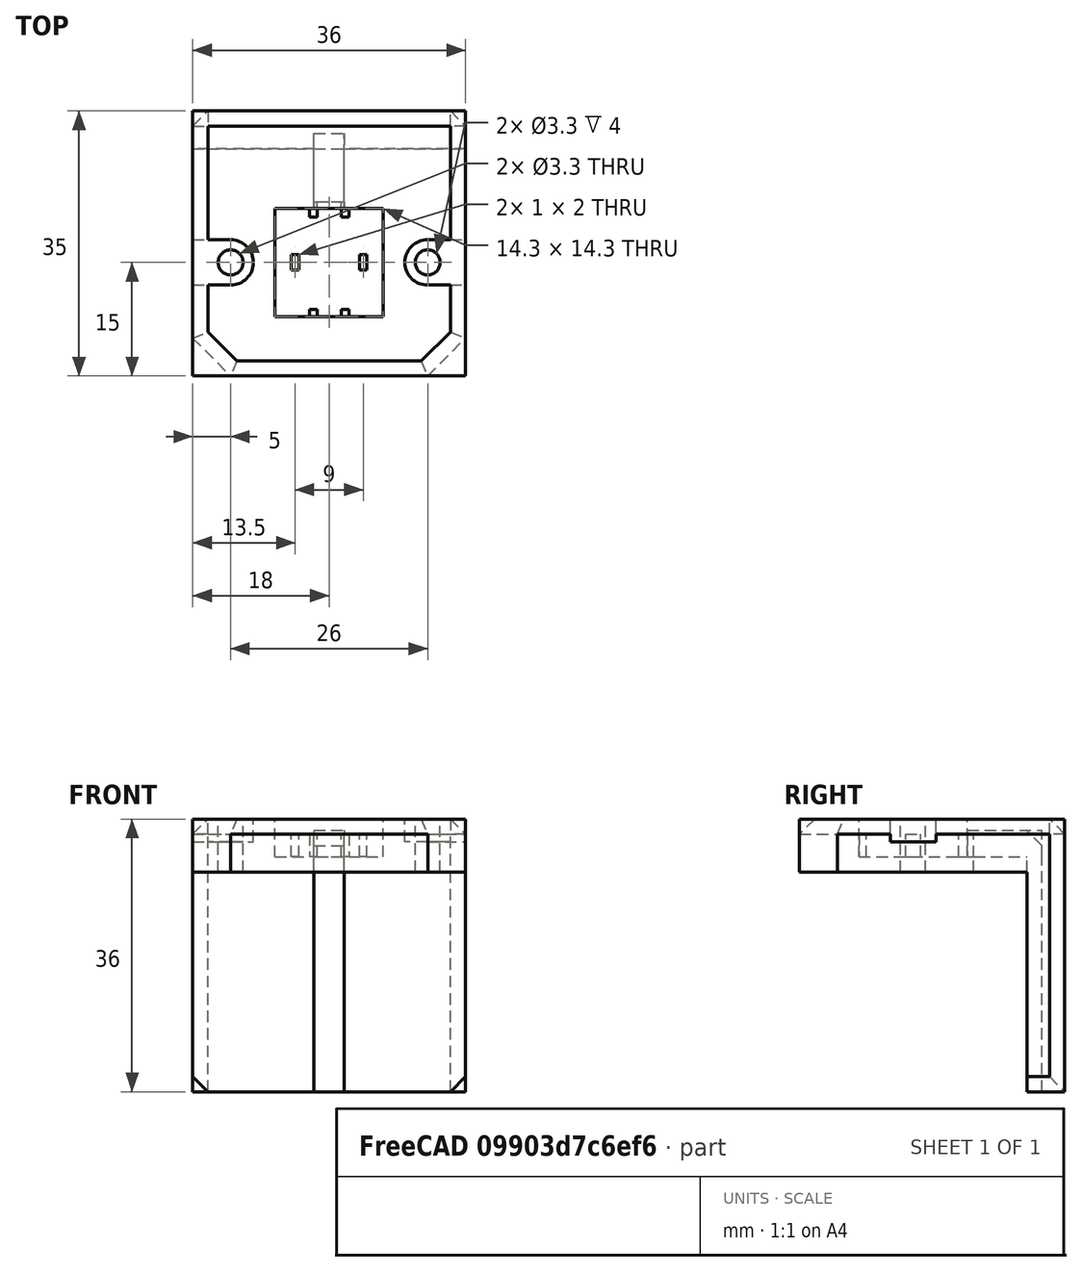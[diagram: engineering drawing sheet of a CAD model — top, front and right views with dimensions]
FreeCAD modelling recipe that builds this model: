
FCSTD DOCUMENT  (FreeCAD 0.18R16146 (Git))
Label: temp-sensor-mount
License: All rights reserved
LicenseURL: http://en.wikipedia.org/wiki/All_rights_reserved
objects: Part::Box×14, Part::MultiFuse×10, Part::Cut×6, Part::Cylinder×4, Part::Chamfer×3, Part::Feature×1
note: 38 computed .brp shape members not serialized (recipe doc carries the construction recipe); baked Part::Feature solids carry a one-line shape summary decoded from their .brp

FEATURE [Part::Box] Box  label="Cube"
  AttacherType = Attacher::AttachEngine3D
  Height = 7
  Length = 36
  Placement = pos=(-18,0,0) rot=(0,0,1;0rad)
  Width = 35
FEATURE [Part::Box] Box001  label="Cube001"
  AttacherType = Attacher::AttachEngine3D
  Height = 36
  Length = 36
  Placement = pos=(-18,30,-29) rot=(0,0,1;0rad)
  Width = 5
FEATURE [Part::Box] Box002  label="Cube002"
  AttacherType = Attacher::AttachEngine3D
  Height = 10
  Length = 14.3
  Placement = pos=(-7.15,7.85,2) rot=(0,0,1;0rad)
  Width = 14.3
FEATURE [Part::Box] Box003  label="Cube003"
  AttacherType = Attacher::AttachEngine3D
  Height = 36
  Length = 4
  Placement = pos=(-2,30,-31) rot=(0,0,1;0rad)
  Width = 2
FEATURE [Part::Box] Box004  label="Cube004"
  AttacherType = Attacher::AttachEngine3D
  Height = 3.5
  Length = 4
  Placement = pos=(-2,20,2) rot=(0,0,1;0rad)
  Width = 12
FEATURE [Part::Box] Box005  label="Cube005"
  AttacherType = Attacher::AttachEngine3D
  Height = 5
  Length = 1
  Placement = pos=(4,14,0) rot=(0,0,1;0rad)
  Width = 2
FEATURE [Part::Box] Box006  label="Cube006"
  AttacherType = Attacher::AttachEngine3D
  Height = 5
  Length = 1
  Placement = pos=(-5,14,0) rot=(0,0,1;0rad)
  Width = 2
FEATURE [Part::Box] Box007  label="Cube007"
  AttacherType = Attacher::AttachEngine3D
  Height = 5
  Length = 1
  Placement = pos=(-2.6,10,0) rot=(0,0,1;0rad)
  Width = 2
FEATURE [Part::Box] Box008  label="Cube008"
  AttacherType = Attacher::AttachEngine3D
  Height = 5
  Length = 1
  Placement = pos=(1.6,10,0) rot=(0,0,1;0rad)
  Width = 2
FEATURE [Part::MultiFuse] Fusion001
  Placement = pos=(0,-3.2,0) rot=(0,0,1;0rad)
  Shapes = -> [Box008,Box007]
FEATURE [Part::Box] Box009  label="Cube009"
  AttacherType = Attacher::AttachEngine3D
  Height = 5
  Length = 1
  Placement = pos=(-2.6,10,0) rot=(0,0,1;0rad)
  Width = 2
FEATURE [Part::Box] Box010  label="Cube010"
  AttacherType = Attacher::AttachEngine3D
  Height = 5
  Length = 1
  Placement = pos=(1.6,10,0) rot=(0,0,1;0rad)
  Width = 2
FEATURE [Part::MultiFuse] Fusion002
  Placement = pos=(0,11,0) rot=(0,0,1;0rad)
  Shapes = -> [Box010,Box009]
FEATURE [Part::Cylinder] Cylinder
  Angle = 360
  AttacherType = Attacher::AttachEngine3D
  Height = 10
  Placement = pos=(-13,15,0) rot=(0,0,1;0rad)
  Radius = 3
FEATURE [Part::Cylinder] Cylinder001
  Angle = 360
  AttacherType = Attacher::AttachEngine3D
  Height = 10
  Placement = pos=(13,15,0) rot=(0,0,1;0rad)
  Radius = 3
FEATURE [Part::Cylinder] Cylinder002
  Angle = 360
  AttacherType = Attacher::AttachEngine3D
  Height = 10
  Placement = pos=(-13,15,0) rot=(0,0,1;0rad)
  Radius = 1.65
FEATURE [Part::Cylinder] Cylinder003
  Angle = 360
  AttacherType = Attacher::AttachEngine3D
  Height = 10
  Placement = pos=(13,15,0) rot=(0,0,1;0rad)
  Radius = 1.65
FEATURE [Part::Box] Box011  label="Cube011"
  AttacherType = Attacher::AttachEngine3D
  Height = 3
  Length = 5
  Placement = pos=(13,12,4) rot=(0,0,1;0rad)
  Width = 6
FEATURE [Part::Box] Box012  label="Cube012"
  AttacherType = Attacher::AttachEngine3D
  Height = 3
  Length = 5
  Placement = pos=(-18,12,4) rot=(0,0,1;0rad)
  Width = 6
FEATURE [Part::MultiFuse] Fusion
  Shapes = -> [Box,Box001]
FEATURE [Part::Cut] Cut
  Base = -> Fusion
  Tool = -> Box002
FEATURE [Part::Cut] Cut001
  Base = -> Cut
  Tool = -> Box003
FEATURE [Part::Cut] Cut002
  Base = -> Cut001
  Tool = -> Box004
FEATURE [Part::MultiFuse] Fusion003
  Shapes = -> [Cylinder002,Cylinder003]
FEATURE [Part::Cut] Cut003
  Base = -> Cut002
  Tool = -> Fusion003
FEATURE [Part::MultiFuse] Fusion004
  Placement = pos=(0,0,4) rot=(0,0,1;0rad)
  Shapes = -> [Cylinder,Cylinder001]
FEATURE [Part::MultiFuse] Fusion005
  Shapes = -> [Box005,Box006]
FEATURE [Part::MultiFuse] Fusion006
  Shapes = -> [Fusion005,Fusion002,Fusion001]
FEATURE [Part::MultiFuse] Fusion007
  Shapes = -> [Cut003,Fusion006]
FEATURE [Part::MultiFuse] Fusion008
  Shapes = -> [Box012,Box011]
FEATURE [Part::MultiFuse] Fusion009
  Shapes = -> [Fusion008,Fusion004]
FEATURE [Part::Feature] Fusion007001  label="Fusion010"
  shape: bbox 36 x 35 x 36 mm, 49 faces (baked)
FEATURE [Part::Chamfer] Chamfer
  Base = -> Fusion007001
  Edges = 2 edges r=5: [Edge18,Edge20]
FEATURE [Part::Chamfer] Chamfer001
  Base = -> Chamfer
  Edges = 10 edges r=2: [Edge1,Edge3,Edge5,Edge7,Edge8,Edge9,Edge10,Edge11,Edge20,Edge30]
FEATURE [Part::Cut] Cut004
  Base = -> Chamfer001
  Tool = -> Fusion009
FEATURE [Part::Box] Box013  label="Cube013"
  AttacherType = Attacher::AttachEngine3D
  Height = 2
  Length = 4
  Placement = pos=(-2,23,0) rot=(0,0,1;0rad)
  Width = 7
FEATURE [Part::Cut] Cut005
  Base = -> Cut004
  Tool = -> Box013
FEATURE [Part::Chamfer] Chamfer002
  Base = -> Cut005
  Edges = 1 edges r=2: [Edge162]
